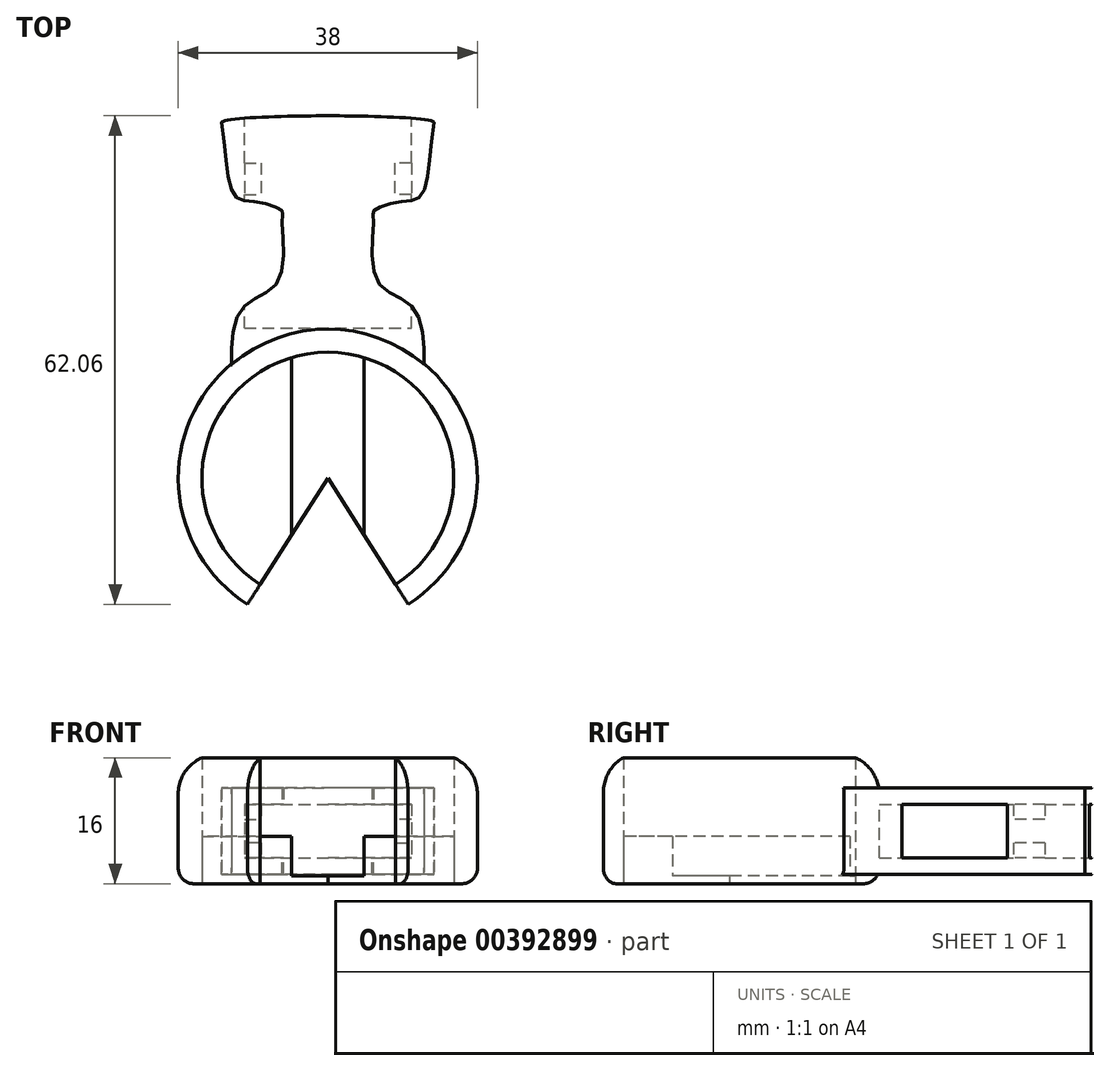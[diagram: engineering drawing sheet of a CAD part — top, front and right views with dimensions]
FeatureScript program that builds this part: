
annotation { "Feature Type Name" : "Feature", "Feature Type Description" : "" }
export const myFeature = defineFeature(function(context is Context, id is Id, definition is map)
    precondition{}
    {
        {
            var Q0;
            Q0=qCreatedBy(makeId("Top.planeOp"),FACE);
            var sketch = newSketch(context, id + "F0", { "sketchPlane" : qUnion([Q0])});
            skCircle(sketch, "E0", {"center": v(0, 0) * mm, "radius": 16 * mm});
            skCircle(sketch, "E1.0", {"center": v(0, 0) * mm, "radius": 19 * mm});
            skLineSegment(sketch, "E2.bottom", {"start": v(-4.6, 16) * mm, "end": v(4.6, 16) * mm});
            skLineSegment(sketch, "E2.top", {"start": v(-4.6, -16) * mm, "end": v(4.6, -16) * mm});
            skLineSegment(sketch, "E2.left", {"start": v(-4.6, 16) * mm, "end": v(-4.6, 15.32) * mm});
            skLineSegment(sketch, "E2.right", {"start": v(4.6, 16) * mm, "end": v(4.6, 15.32) * mm});
            skLineSegment(sketch, "E3", {"start": v(-4.6, 15.32) * mm, "end": v(-4.6, -15.32) * mm});
            skLineSegment(sketch, "E4", {"start": v(4.6, 15.32) * mm, "end": v(4.6, -15.32) * mm});
            skLineSegment(sketch, "E5", {"start": v(4.6, -15.32) * mm, "end": v(4.6, -16) * mm});
            skLineSegment(sketch, "E6", {"start": v(-4.6, -15.32) * mm, "end": v(-4.6, -16) * mm});
            skLineSegment(sketch, "E7", {"start": v(0, 0) * mm, "end": v(-15.4, -24.17) * mm});
            skLineSegment(sketch, "E8", {"start": v(-15.4, -24.17) * mm, "end": v(15.4, -24.17) * mm});
            skLineSegment(sketch, "E9", {"start": v(15.4, -24.17) * mm, "end": v(0, 0) * mm});
            skPoint(sketch, "E10", {"position": v(0, -24.17) * mm});
            skSolve(sketch);
        }
        {
            var Q0;
            {var subQ3=sQuery(id+"F0.wireOp",EDGE,"E9");var subQ7=sQuery(id+"F0.wireOp",EDGE,"E7");var subQ10=makeQuery(id+"F0.imprint","INTERSECT",VERTEX,{"derivedFrom":[subQ7,subQ3]});Q0=makeQuery(id+"F0.imprint","IMPRINT",FACE,{"disambiguationData":[TD([[makeQuery(id+"F0.imprint","IMPRINT",EDGE,{"disambiguationData":[TD([[subQ10,-1.0]])],"derivedFrom":subQ7}),-1.0]])]});}
            extrude(context, id + "F1", {"entities" : qUnion([Q0]), "depth" : 1 * mm});
        }
        {
            var Q0;
            {var subQ1=sQuery(id+"F0.wireOp",EDGE,"E0");var subQ3=sQuery(id+"F0.wireOp",EDGE,"E9");var subQ4=makeQuery(id+"F0.imprint","INTERSECT",VERTEX,{"derivedFrom":[subQ1,subQ3]});Q0=makeQuery(id+"F0.imprint","IMPRINT",FACE,{"disambiguationData":[TD([[makeQuery(id+"F0.imprint","IMPRINT",EDGE,{"disambiguationData":[TD([[subQ4,-1.0]])],"derivedFrom":subQ3}),-1.0]])]});}
            var Q1;
            {var subQ1=sQuery(id+"F0.wireOp",EDGE,"E0");var subQ3=sQuery(id+"F0.wireOp",EDGE,"E7");var subQ4=makeQuery(id+"F0.imprint","INTERSECT",VERTEX,{"derivedFrom":[subQ1,subQ3]});Q1=makeQuery(id+"F0.imprint","IMPRINT",FACE,{"disambiguationData":[TD([[makeQuery(id+"F0.imprint","IMPRINT",EDGE,{"disambiguationData":[TD([[subQ4,1.0]])],"derivedFrom":subQ3}),-1.0]])]});}
            extrude(context, id + "F2", {"entities" : qUnion([Q0, Q1]), "operationType" : NewBodyOperationType.ADD, "depth" : 6 * mm});
        }
        {
            var Q0;
            {var subQ0=sQuery(id+"F0.wireOp",EDGE,"E2.left");Q0=makeQuery(id+"F0.imprint","IMPRINT",FACE,{"disambiguationData":[TD([[makeQuery(id+"F0.imprint","IMPRINT",EDGE,{"derivedFrom":subQ0}),1.0]])]});}
            var Q1;
            {var subQ0=sQuery(id+"F0.wireOp",EDGE,"E2.right");Q1=makeQuery(id+"F0.imprint","IMPRINT",FACE,{"disambiguationData":[TD([[makeQuery(id+"F0.imprint","IMPRINT",EDGE,{"derivedFrom":subQ0}),-1.0]])]});}
            var Q2;
            {var subQ0=sQuery(id+"F0.wireOp",EDGE,"E2.left");Q2=makeQuery(id+"F0.imprint","IMPRINT",FACE,{"disambiguationData":[TD([[makeQuery(id+"F0.imprint","IMPRINT",EDGE,{"derivedFrom":subQ0}),-1.0]])]});}
            extrude(context, id + "F3", {"entities" : qUnion([Q0, Q1, Q2]), "depth" : 16 * mm});
        }
        {
            var Q0;
            Q0=qCreatedBy(makeId("Top.planeOp"),FACE);
            cPlane(context, id + "F4", {"entities" : qUnion([Q0]), "cplaneType" : CPlaneType.OFFSET, "offset" : 6.7 * mm, "width" : 150 * mm, "height" : 150 * mm});
        }
        {
            var Q0;
            Q0=makeQuery(id+"F3.opExtrude","CAP_EDGE",EDGE,{"disambiguationData":[OSD([sQuery(id+"F0.wireOp",EDGE,"E1.0")])],"isStart":false});
            fillet(context, id + "F5", {"entities" : qUnion([Q0]), "radius" : 5 * mm, "tangentPropagation" : true, "allowEdgeOverflow" : false});
        }
        {
            var Q0;
            Q0=makeQuery(id+"F3.opExtrude","CAP_EDGE",EDGE,{"disambiguationData":[OSD([sQuery(id+"F0.wireOp",EDGE,"E1.0")])],"isStart":true});
            fillet(context, id + "F6", {"entities" : qUnion([Q0]), "radius" : 2 * mm, "tangentPropagation" : true, "allowEdgeOverflow" : false});
        }
        {
            var Q0;
            {var subQ0=sQuery(id+"F0.wireOp",EDGE,"E1.0");Q0=makeQuery(id+"F6.opFillet","BLEND_EDGE",EDGE,{"blendedFrom":[makeQuery(id+"F3.opExtrude","CAP_EDGE",EDGE,{"disambiguationData":[OSD([subQ0])],"isStart":true}),makeQuery(id+"F3.opExtrude","SWEPT_FACE",FACE,{"disambiguationData":[OSD([subQ0])]})],"blendedInto":[makeQuery(id+"F3.opExtrude","SWEPT_FACE",FACE,{"disambiguationData":[OSD([subQ0])]})]});}
            cPoint(context, id + "F7", {"entities" : qUnion([Q0]), "parameter" : 0.5});
        }
        {
            var Q0;
            Q0 = qCreatedBy(id + "F7" ,VERTEX);
            var Q1;
            Q1=qCreatedBy(makeId("Front.planeOp"),FACE);
            cPlane(context, id + "F8", {"entities" : qUnion([Q0, Q1]), "cplaneType" : CPlaneType.PLANE_POINT, "offset" : 16 * mm, "oppositeDirection" : true, "width" : 150 * mm, "height" : 150 * mm});
        }
        {
            var Q0;
            Q0=qCreatedBy(id+"F4.planeOp",FACE);
            var sketch = newSketch(context, id + "F9", { "sketchPlane" : qUnion([Q0])});
            skLineSegment(sketch, "E11", {"start": v(6.79, 19) * mm, "end": v(-0.09, 19) * mm});
            skPoint(sketch, "E12", {"position": v(5.8, 33.24) * mm});
            skPoint(sketch, "E13", {"position": v(11.88, 35.94) * mm});
            skPoint(sketch, "E14", {"position": v(13.5, 45.14) * mm});
            skPoint(sketch, "E15", {"position": v(11, 21.44) * mm});
            skPoint(sketch, "E16", {"position": v(12.15, 13.26) * mm});
            skFitSpline(sketch, "E17", {"points": [v(12.15, 13.26) * mm, v(11, 21.44) * mm, v(6.3, 25.08) * mm, v(5.8, 33.24) * mm, v(5.84, 34.03) * mm, v(9.11, 35.12) * mm, v(11.88, 35.94) * mm, v(13.5, 45.14) * mm], "startDerivative": vector(1.56, 36.86) * mm, "endDerivative": vector(10.4, 54.61) * mm});
            skLineSegment(sketch, "E18", {"start": v(12.15, 13.26) * mm, "end": v(12.15, 12.46) * mm});
            skLineSegment(sketch, "E19", {"start": v(12.15, 12.46) * mm, "end": v(0, 18.03) * mm});
            skFitSpline(sketch, "E20", {"points": [v(13.5, 45.14) * mm, v(0, 46.04) * mm], "startDerivative": vector(0.8, 2.32) * mm, "endDerivative": vector(-8.8, 0.01) * mm});
            skPoint(sketch, "E21.MirrorP", {"position": v(-5.8, 33.24) * mm});
            skPoint(sketch, "E22.MirrorP", {"position": v(-13.5, 45.14) * mm});
            skFitSpline(sketch, "E23.MirrorCS", {"points": [v(-13.5, 45.14) * mm, v(0, 46.04) * mm], "startDerivative": vector(-0.8, 2.32) * mm, "endDerivative": vector(8.8, 0.01) * mm});
            skPoint(sketch, "E24.MirrorP", {"position": v(-11, 21.44) * mm});
            skPoint(sketch, "E25.MirrorP", {"position": v(-12.15, 13.26) * mm});
            skPoint(sketch, "E26.MirrorP", {"position": v(-11.88, 35.94) * mm});
            skLineSegment(sketch, "E27.MirrorCS", {"start": v(-12.15, 12.46) * mm, "end": v(0, 18.03) * mm});
            skLineSegment(sketch, "E28.MirrorCS", {"start": v(-12.15, 13.26) * mm, "end": v(-12.15, 12.46) * mm});
            skFitSpline(sketch, "E29.MirrorCS", {"points": [v(-12.15, 13.26) * mm, v(-11, 21.44) * mm, v(-6.3, 25.08) * mm, v(-5.8, 33.24) * mm, v(-5.84, 34.03) * mm, v(-9.11, 35.12) * mm, v(-11.88, 35.94) * mm, v(-13.5, 45.14) * mm], "startDerivative": vector(-1.56, 36.86) * mm, "endDerivative": vector(-10.4, 54.61) * mm});
            skSolve(sketch);
        }
        {
            var Q0;
            Q0=makeQuery(id+"F9.imprint","IMPRINT",FACE,{"disambiguationData":[TD([[makeQuery(id+"F9.imprint","IMPRINT",EDGE,{"derivedFrom":sQuery(id+"F9.wireOp",EDGE,"E17")}),1.0]])]});
            extrude(context, id + "F10", {"entities" : qUnion([Q0]), "operationType" : NewBodyOperationType.ADD, "endBound" : BoundingType.SYMMETRIC, "depth" : 11 * mm});
        }
        {
            var Q0;
            Q0=makeQuery(id+"F10.opExtrude","SWEPT_EDGE",EDGE,{"disambiguationData":[OSD([sQuery(id+"F9.wireOp",EDGE,"E20"),sQuery(id+"F9.wireOp",EDGE,"E23.MirrorCS")])]});
            cPoint(context, id + "F11", {"entities" : qUnion([Q0]), "parameter" : 0.5});
        }
        {
            var Q0;
            Q0 = qCreatedBy(id + "F11" ,VERTEX);
            var Q1;
            Q1=qCreatedBy(id+"F8.planeOp",FACE);
            cPlane(context, id + "F12", {"entities" : qUnion([Q0, Q1]), "cplaneType" : CPlaneType.PLANE_POINT, "offset" : 25 * mm, "width" : 150 * mm, "height" : 150 * mm});
        }
        {
            var Q0;
            Q0=qCreatedBy(id+"F12.planeOp",FACE);
            var sketch = newSketch(context, id + "F13", { "sketchPlane" : qUnion([Q0])});
            skPoint(sketch, "E30", {"position": v(0, 6.7) * mm});
            skLineSegment(sketch, "E31.bottom", {"start": v(-10.6, 3.3) * mm, "end": v(10.6, 3.3) * mm});
            skLineSegment(sketch, "E31.top", {"start": v(-10.6, 10.1) * mm, "end": v(10.6, 10.1) * mm});
            skLineSegment(sketch, "E31.left", {"start": v(-10.6, 3.3) * mm, "end": v(-10.6, 10.1) * mm});
            skLineSegment(sketch, "E31.right", {"start": v(10.6, 3.3) * mm, "end": v(10.6, 10.1) * mm});
            skSolve(sketch);
        }
        {
            var Q0;
            Q0 = qSketchRegion(id + "F13", true);
            extrude(context, id + "F14", {"entities" : qUnion([Q0]), "operationType" : NewBodyOperationType.REMOVE, "depth" : 27 * mm});
        }
        {
            var Q0;
            Q0=qCreatedBy(id+"F12.planeOp",FACE);
            cPlane(context, id + "F15", {"entities" : qUnion([Q0]), "cplaneType" : CPlaneType.OFFSET, "offset" : 10 * mm, "width" : 150 * mm, "height" : 150 * mm});
        }
        {
            var Q0;
            Q0=qCreatedBy(id+"F15.planeOp",FACE);
            var sketch = newSketch(context, id + "F16", { "sketchPlane" : qUnion([Q0])});
            skLineSegment(sketch, "E32.bottom", {"start": v(-10.6, 10.1) * mm, "end": v(-8.5, 10.1) * mm});
            skLineSegment(sketch, "E32.top", {"start": v(-10.6, 8.2) * mm, "end": v(-8.5, 8.2) * mm});
            skLineSegment(sketch, "E32.left", {"start": v(-10.6, 10.1) * mm, "end": v(-10.6, 8.2) * mm});
            skLineSegment(sketch, "E32.right", {"start": v(-8.5, 10.1) * mm, "end": v(-8.5, 8.2) * mm});
            skLineSegment(sketch, "E33.bottom", {"start": v(-8.5, 5.2) * mm, "end": v(-10.6, 5.2) * mm});
            skLineSegment(sketch, "E33.top", {"start": v(-8.5, 3.3) * mm, "end": v(-10.6, 3.3) * mm});
            skLineSegment(sketch, "E33.left", {"start": v(-8.5, 5.2) * mm, "end": v(-8.5, 3.3) * mm});
            skLineSegment(sketch, "E33.right", {"start": v(-10.6, 5.2) * mm, "end": v(-10.6, 3.3) * mm});
            skLineSegment(sketch, "E34.MirrorCS", {"start": v(8.5, 10.1) * mm, "end": v(8.5, 8.2) * mm});
            skLineSegment(sketch, "E35.MirrorCS", {"start": v(10.6, 8.2) * mm, "end": v(8.5, 8.2) * mm});
            skLineSegment(sketch, "E36.MirrorCS", {"start": v(8.5, 5.2) * mm, "end": v(10.6, 5.2) * mm});
            skLineSegment(sketch, "E37.MirrorCS", {"start": v(8.5, 5.2) * mm, "end": v(8.5, 3.3) * mm});
            skLineSegment(sketch, "E38.MirrorCS", {"start": v(10.6, 10.1) * mm, "end": v(10.6, 8.2) * mm});
            skLineSegment(sketch, "E39.MirrorCS", {"start": v(10.6, 10.1) * mm, "end": v(8.5, 10.1) * mm});
            skLineSegment(sketch, "E40.MirrorCS", {"start": v(10.6, 5.2) * mm, "end": v(10.6, 3.3) * mm});
            skLineSegment(sketch, "E41.MirrorCS", {"start": v(8.5, 3.3) * mm, "end": v(10.6, 3.3) * mm});
            skSolve(sketch);
        }
        {
            var Q0;
            Q0=makeQuery(id+"F16.imprint","IMPRINT",FACE,{"disambiguationData":[TD([[makeQuery(id+"F16.imprint","IMPRINT",EDGE,{"derivedFrom":sQuery(id+"F16.wireOp",EDGE,"E33.bottom")}),1.0]])]});
            var Q1;
            Q1=makeQuery(id+"F16.imprint","IMPRINT",FACE,{"disambiguationData":[TD([[makeQuery(id+"F16.imprint","IMPRINT",EDGE,{"derivedFrom":sQuery(id+"F16.wireOp",EDGE,"E32.bottom")}),-1.0]])]});
            var Q2;
            Q2=makeQuery(id+"F16.imprint","IMPRINT",FACE,{"disambiguationData":[TD([[makeQuery(id+"F16.imprint","IMPRINT",EDGE,{"derivedFrom":sQuery(id+"F16.wireOp",EDGE,"E34.MirrorCS")}),1.0]])]});
            var Q3;
            Q3=makeQuery(id+"F16.imprint","IMPRINT",FACE,{"disambiguationData":[TD([[makeQuery(id+"F16.imprint","IMPRINT",EDGE,{"derivedFrom":sQuery(id+"F16.wireOp",EDGE,"E36.MirrorCS")}),-1.0]])]});
            extrude(context, id + "F17", {"entities" : qUnion([Q0, Q1, Q2, Q3]), "operationType" : NewBodyOperationType.ADD, "oppositeDirection" : true, "depth" : 4 * mm});
        }
    });
